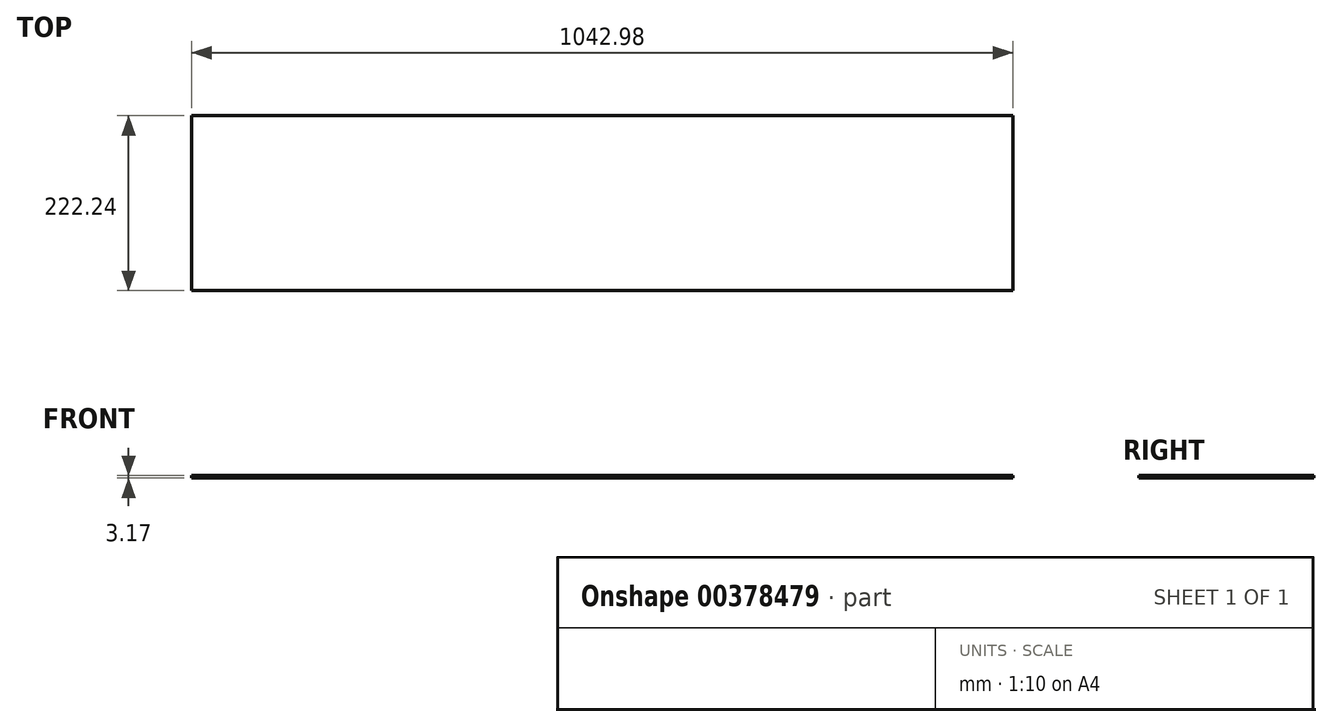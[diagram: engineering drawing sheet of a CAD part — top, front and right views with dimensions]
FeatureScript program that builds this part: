
annotation { "Feature Type Name" : "Feature", "Feature Type Description" : "" }
export const myFeature = defineFeature(function(context is Context, id is Id, definition is map)
    precondition{}
    {
        {
            var Q0;
            Q0=qCreatedBy(makeId("Top.planeOp"),FACE);
            var sketch = newSketch(context, id + "F0", { "sketchPlane" : qUnion([Q0])});
            skLineSegment(sketch, "E0.bottom", {"start": v(521.5, -111.12) * mm, "end": v(-521.5, -111.13) * mm});
            skLineSegment(sketch, "E0.top", {"start": v(521.5, 111.12) * mm, "end": v(-521.5, 111.12) * mm});
            skLineSegment(sketch, "E0.left", {"start": v(521.5, -111.12) * mm, "end": v(521.5, 111.13) * mm});
            skLineSegment(sketch, "E0.right", {"start": v(-521.5, -111.13) * mm, "end": v(-521.5, 111.12) * mm});
            skPoint(sketch, "E0.middle", {"position": v(0, 0) * mm});
            skSolve(sketch);
        }
        {
            var Q0;
            Q0=makeQuery(id+"F0.imprint","IMPRINT",FACE,{"disambiguationData":[TD([[makeQuery(id+"F0.imprint","IMPRINT",EDGE,{"derivedFrom":sQuery(id+"F0.wireOp",EDGE,"E0.bottom")}),-1.0]])]});
            extrude(context, id + "F1", {"entities" : qUnion([Q0]), "depth" : 3.17 * mm});
        }
    });
